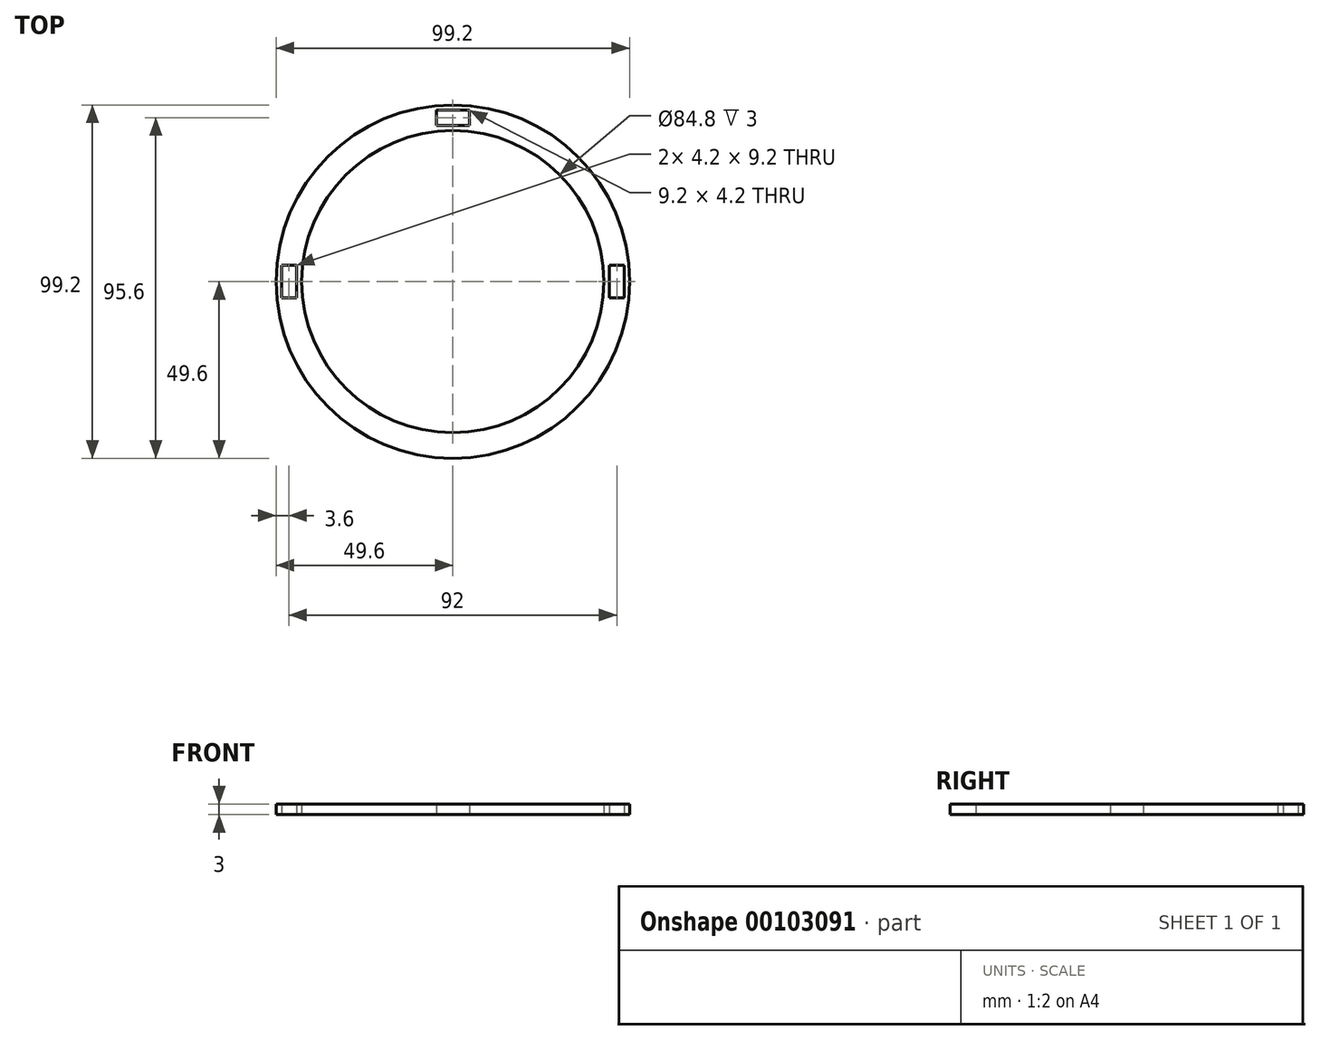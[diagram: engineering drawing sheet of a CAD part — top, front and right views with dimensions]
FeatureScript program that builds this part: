
annotation { "Feature Type Name" : "Feature", "Feature Type Description" : "" }
export const myFeature = defineFeature(function(context is Context, id is Id, definition is map)
    precondition{}
    {
        {
            var Q0;
            Q0=qCreatedBy(makeId("Top.planeOp"),FACE);
            var sketch = newSketch(context, id + "F0", { "sketchPlane" : qUnion([Q0])});
            skCircle(sketch, "E0", {"center": v(0, 0) * mm, "radius": 42.4 * mm});
            skCircle(sketch, "E1", {"center": v(0, 0) * mm, "radius": 49.6 * mm});
            skLineSegment(sketch, "E2", {"start": v(-49.6, 0) * mm, "end": v(-42.4, 0) * mm, "construction": true});
            skLineSegment(sketch, "E3", {"start": v(0, 49.6) * mm, "end": v(0, 42.4) * mm, "construction": true});
            skLineSegment(sketch, "E4", {"start": v(49.6, 0) * mm, "end": v(42.4, 0) * mm, "construction": true});
            skLineSegment(sketch, "E5.bottom", {"start": v(-43.9, -4.6) * mm, "end": v(-48.1, -4.6) * mm});
            skLineSegment(sketch, "E5.top", {"start": v(-43.9, 4.6) * mm, "end": v(-48.1, 4.6) * mm});
            skLineSegment(sketch, "E5.left", {"start": v(-43.9, -4.6) * mm, "end": v(-43.9, 4.6) * mm});
            skLineSegment(sketch, "E5.right", {"start": v(-48.1, -4.6) * mm, "end": v(-48.1, 4.6) * mm});
            skPoint(sketch, "E5.middle", {"position": v(-46, 0) * mm});
            skLineSegment(sketch, "E6.bottom", {"start": v(-4.6, 43.9) * mm, "end": v(4.6, 43.9) * mm});
            skLineSegment(sketch, "E6.top", {"start": v(-4.6, 48.1) * mm, "end": v(4.6, 48.1) * mm});
            skLineSegment(sketch, "E6.left", {"start": v(-4.6, 43.9) * mm, "end": v(-4.6, 48.1) * mm});
            skLineSegment(sketch, "E6.right", {"start": v(4.6, 43.9) * mm, "end": v(4.6, 48.1) * mm});
            skPoint(sketch, "E6.middle", {"position": v(0, 46) * mm});
            skLineSegment(sketch, "E7.bottom", {"start": v(48.1, -4.6) * mm, "end": v(43.9, -4.6) * mm});
            skLineSegment(sketch, "E7.top", {"start": v(48.1, 4.6) * mm, "end": v(43.9, 4.6) * mm});
            skLineSegment(sketch, "E7.left", {"start": v(48.1, -4.6) * mm, "end": v(48.1, 4.6) * mm});
            skLineSegment(sketch, "E7.right", {"start": v(43.9, -4.6) * mm, "end": v(43.9, 4.6) * mm});
            skPoint(sketch, "E7.middle", {"position": v(46, 0) * mm});
            skCircle(sketch, "E8", {"center": v(0, 0) * mm, "radius": 46 * mm, "construction": true});
            skSolve(sketch);
        }
        {
            var Q0;
            Q0 = qSketchRegion(id + "F0", true);
            extrude(context, id + "F1", {"entities" : qUnion([Q0]), "depth" : 3 * mm});
        }
    });
